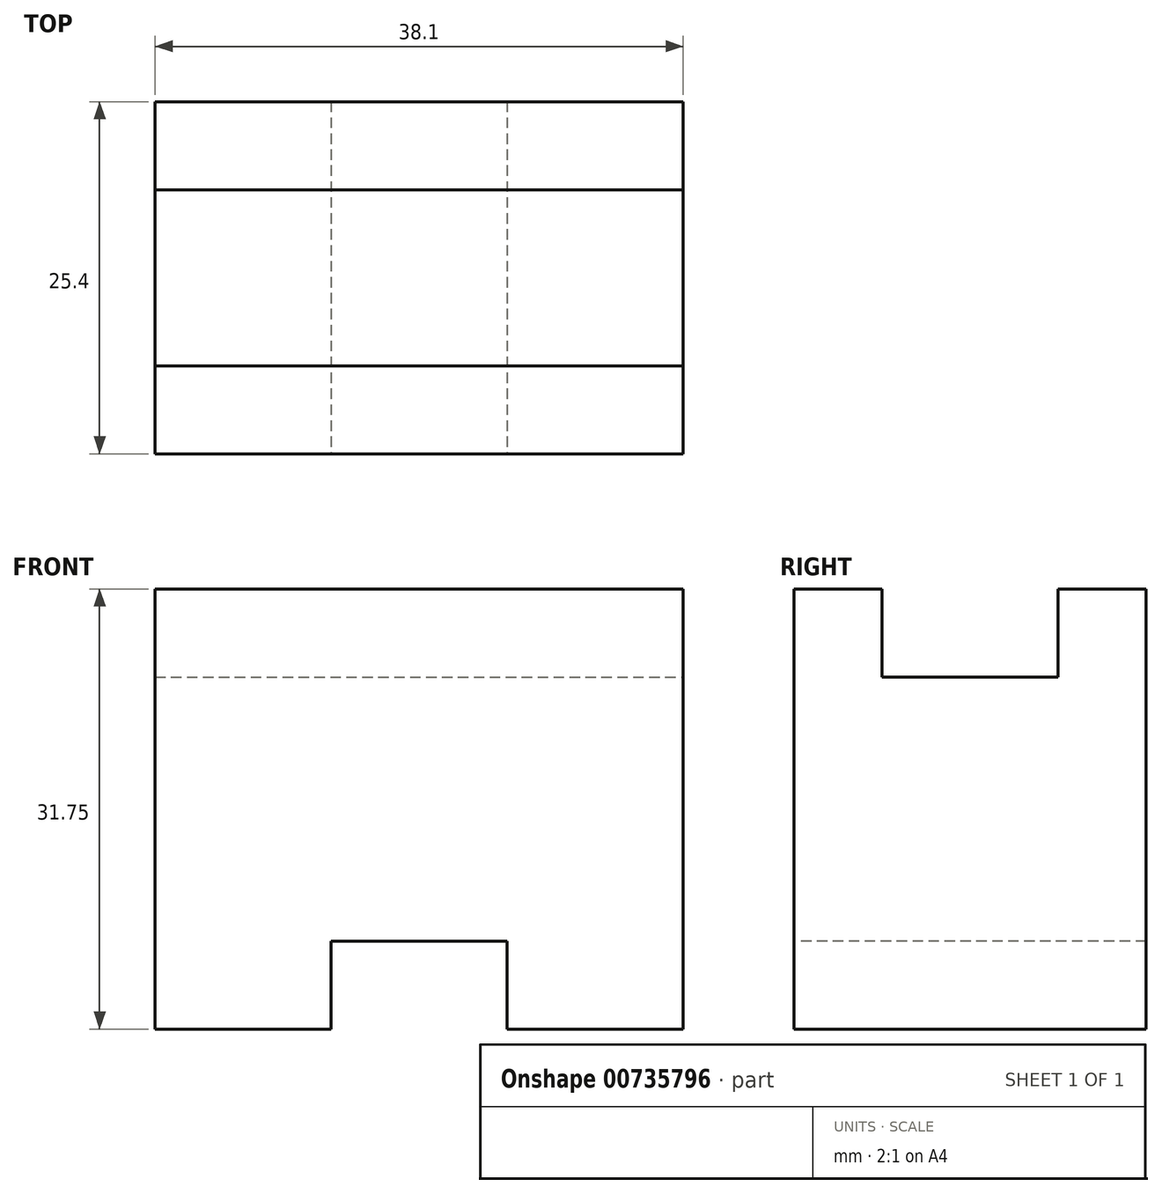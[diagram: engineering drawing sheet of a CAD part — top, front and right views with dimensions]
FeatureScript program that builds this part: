
annotation { "Feature Type Name" : "Feature", "Feature Type Description" : "" }
export const myFeature = defineFeature(function(context is Context, id is Id, definition is map)
    precondition{}
    {
        {
            var Q0;
            Q0=qCreatedBy(makeId("Right.planeOp"),FACE);
            var sketch = newSketch(context, id + "F0", { "sketchPlane" : qUnion([Q0])});
            skLineSegment(sketch, "E0", {"start": v(0, 31.75) * mm, "end": v(0, 0) * mm});
            skLineSegment(sketch, "E1", {"start": v(0, 0) * mm, "end": v(25.4, 0) * mm});
            skLineSegment(sketch, "E2", {"start": v(25.4, 0) * mm, "end": v(25.4, 31.75) * mm});
            skLineSegment(sketch, "E3", {"start": v(25.4, 31.75) * mm, "end": v(0, 31.75) * mm});
            skSolve(sketch);
        }
        {
            var Q0;
            Q0=makeQuery(id+"F0.imprint","IMPRINT",FACE,{"disambiguationData":[TD([[makeQuery(id+"F0.imprint","IMPRINT",EDGE,{"derivedFrom":sQuery(id+"F0.wireOp",EDGE,"E0")}),1.0]])]});
            extrude(context, id + "F1", {"entities" : qUnion([Q0]), "depth" : 38.1 * mm, "offsetDistance" : 25.4 * mm});
        }
        {
            var Q0;
            Q0=makeQuery(id+"F1.opExtrude","SWEPT_FACE",FACE,{"disambiguationData":[OSD([sQuery(id+"F0.wireOp",EDGE,"E0")])]});
            var sketch = newSketch(context, id + "F2", { "sketchPlane" : qUnion([Q0])});
            skLineSegment(sketch, "E4", {"start": v(12.7, 0) * mm, "end": v(12.7, 6.35) * mm});
            skLineSegment(sketch, "E5", {"start": v(12.7, 6.35) * mm, "end": v(25.4, 6.35) * mm});
            skLineSegment(sketch, "E6", {"start": v(25.4, 6.35) * mm, "end": v(25.4, 0) * mm});
            skLineSegment(sketch, "E7", {"start": v(25.4, 0) * mm, "end": v(12.7, 0) * mm});
            skSolve(sketch);
        }
        {
            var Q0;
            Q0=makeQuery(id+"F2.imprint","IMPRINT",FACE,{"disambiguationData":[TD([[makeQuery(id+"F2.imprint","IMPRINT",EDGE,{"derivedFrom":sQuery(id+"F2.wireOp",EDGE,"E4")}),-1.0]])]});
            extrude(context, id + "F3", {"entities" : qUnion([Q0]), "operationType" : NewBodyOperationType.REMOVE, "oppositeDirection" : true, "depth" : 25.4 * mm, "offsetDistance" : 25.4 * mm});
        }
        {
            var Q0;
            Q0=makeQuery(id+"F1.opExtrude","CAP_FACE",FACE,{"disambiguationData":[OSD([sQuery(id+"F0.wireOp",EDGE,"E0"),sQuery(id+"F0.wireOp",EDGE,"E1"),sQuery(id+"F0.wireOp",EDGE,"E2"),sQuery(id+"F0.wireOp",EDGE,"E3")])],"isStart":false});
            var sketch = newSketch(context, id + "F4", { "sketchPlane" : qUnion([Q0])});
            skLineSegment(sketch, "E8", {"start": v(6.35, 31.75) * mm, "end": v(6.35, 25.4) * mm});
            skLineSegment(sketch, "E9", {"start": v(6.35, 25.4) * mm, "end": v(19.05, 25.4) * mm});
            skLineSegment(sketch, "E10", {"start": v(19.05, 25.4) * mm, "end": v(19.05, 31.75) * mm});
            skLineSegment(sketch, "E11", {"start": v(19.05, 31.75) * mm, "end": v(6.35, 31.75) * mm});
            skSolve(sketch);
        }
        {
            var Q0;
            Q0=makeQuery(id+"F4.imprint","IMPRINT",FACE,{"disambiguationData":[TD([[makeQuery(id+"F4.imprint","IMPRINT",EDGE,{"derivedFrom":sQuery(id+"F4.wireOp",EDGE,"E8")}),1.0]])]});
            extrude(context, id + "F5", {"entities" : qUnion([Q0]), "operationType" : NewBodyOperationType.REMOVE, "oppositeDirection" : true, "depth" : 38.1 * mm, "offsetDistance" : 25.4 * mm});
        }
    });
